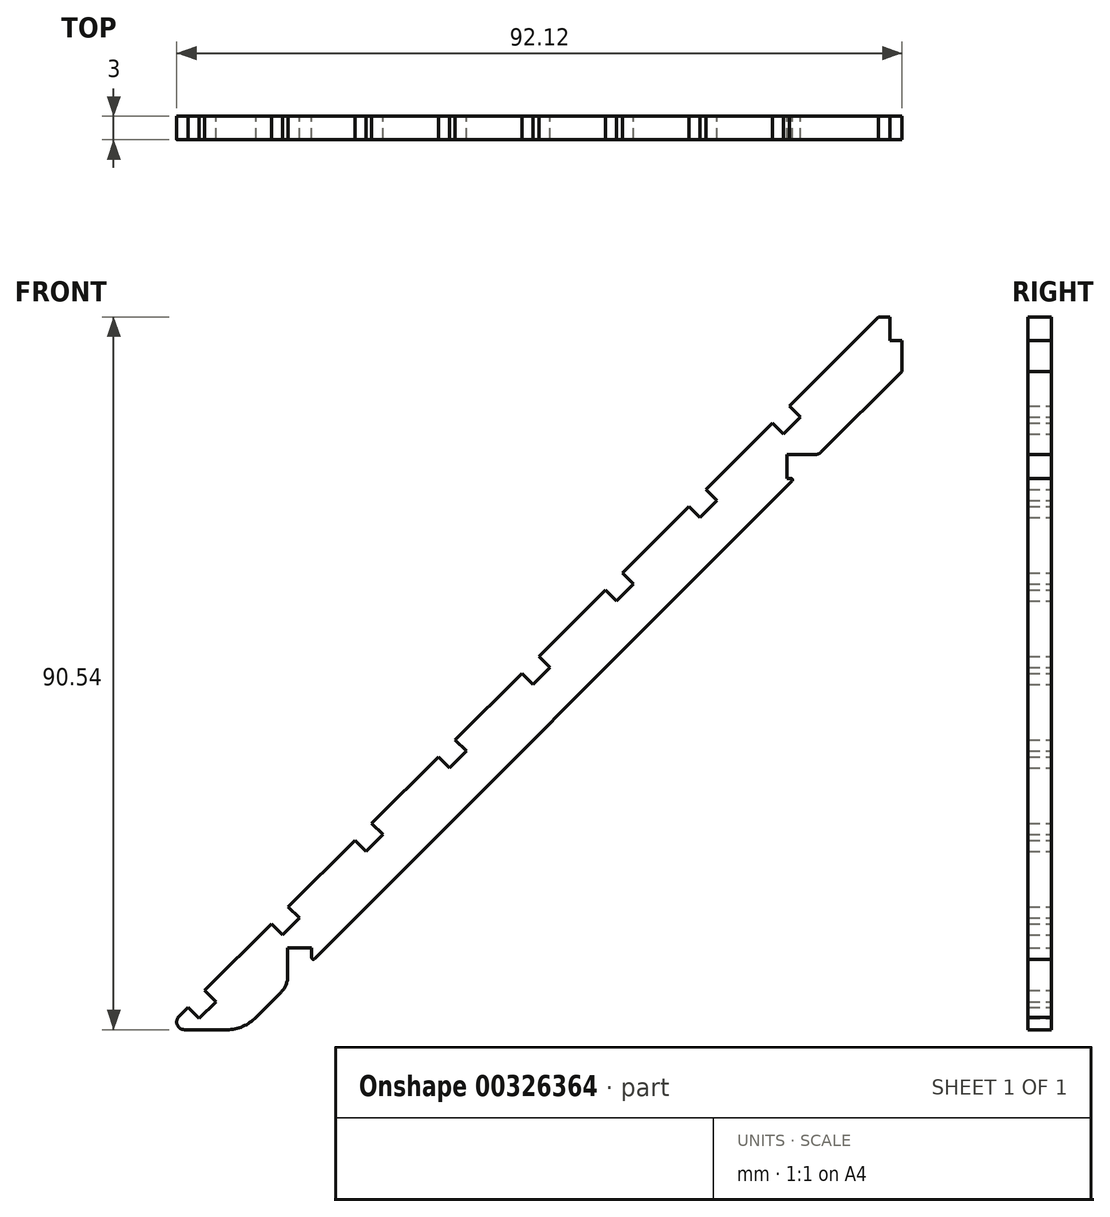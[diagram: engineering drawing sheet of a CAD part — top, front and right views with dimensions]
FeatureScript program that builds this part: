
annotation { "Feature Type Name" : "Feature", "Feature Type Description" : "" }
export const myFeature = defineFeature(function(context is Context, id is Id, definition is map)
    precondition{}
    {
        {
            var Q0;
            Q0=qCreatedBy(makeId("Front.planeOp"),FACE);
            var sketch = newSketch(context, id + "F0", { "sketchPlane" : qUnion([Q0])});
            skLineSegment(sketch, "E0", {"start": v(-77.95, 1.26) * mm, "end": v(-69.5, 9.72) * mm});
            skLineSegment(sketch, "E1", {"start": v(-80.1, -0.89) * mm, "end": v(-88.56, -9.34) * mm});
            skLineSegment(sketch, "E2", {"start": v(-85.7, -14.32) * mm, "end": v(-91.12, -14.32) * mm});
            skLineSegment(sketch, "E3", {"start": v(-90.7, -11.5) * mm, "end": v(-89.3, -12.9) * mm});
            skLineSegment(sketch, "E4", {"start": v(-89.3, -12.9) * mm, "end": v(-87.14, -10.76) * mm});
            skLineSegment(sketch, "E5", {"start": v(-78.69, -2.3) * mm, "end": v(-76.54, -0.15) * mm});
            skLineSegment(sketch, "E6", {"start": v(-80.1, -0.89) * mm, "end": v(-78.69, -2.3) * mm});
            skPoint(sketch, "E7", {"position": v(-69.5, 9.72) * mm});
            skPoint(sketch, "E8", {"position": v(-58.89, 20.33) * mm});
            skPoint(sketch, "E9", {"position": v(-48.28, 30.93) * mm});
            skPoint(sketch, "E10", {"position": v(-37.67, 41.54) * mm});
            skPoint(sketch, "E11", {"position": v(-27.07, 52.15) * mm});
            skPoint(sketch, "E12", {"position": v(-16.46, 62.75) * mm});
            skLineSegment(sketch, "E13", {"start": v(-87.14, -10.76) * mm, "end": v(-88.56, -9.34) * mm});
            skLineSegment(sketch, "E14", {"start": v(-69.5, 9.72) * mm, "end": v(-68.08, 8.3) * mm});
            skLineSegment(sketch, "E15", {"start": v(-58.89, 20.33) * mm, "end": v(-57.47, 18.91) * mm});
            skLineSegment(sketch, "E16", {"start": v(-48.28, 30.93) * mm, "end": v(-46.87, 29.52) * mm});
            skLineSegment(sketch, "E17", {"start": v(-37.67, 41.54) * mm, "end": v(-36.26, 40.12) * mm});
            skLineSegment(sketch, "E18", {"start": v(-27.07, 52.15) * mm, "end": v(-25.65, 50.73) * mm});
            skLineSegment(sketch, "E19", {"start": v(-16.46, 62.75) * mm, "end": v(-15.05, 61.34) * mm});
            skLineSegment(sketch, "E20", {"start": v(-77.95, 1.26) * mm, "end": v(-76.54, -0.15) * mm});
            skLineSegment(sketch, "E21", {"start": v(-67.34, 11.87) * mm, "end": v(-65.93, 10.45) * mm});
            skLineSegment(sketch, "E22", {"start": v(-56.74, 22.48) * mm, "end": v(-55.32, 21.06) * mm});
            skLineSegment(sketch, "E23", {"start": v(-46.13, 33.08) * mm, "end": v(-44.72, 31.67) * mm});
            skLineSegment(sketch, "E24", {"start": v(-35.53, 43.69) * mm, "end": v(-34.11, 42.27) * mm});
            skLineSegment(sketch, "E25", {"start": v(-24.92, 54.3) * mm, "end": v(-23.5, 52.88) * mm});
            skLineSegment(sketch, "E26", {"start": v(-14.31, 64.9) * mm, "end": v(-12.9, 63.49) * mm});
            skLineSegment(sketch, "E27", {"start": v(-3, 76.22) * mm, "end": v(-1.52, 76.22) * mm});
            skLineSegment(sketch, "E28", {"start": v(-1.52, 73.21) * mm, "end": v(-1.52, 76.22) * mm});
            skLineSegment(sketch, "E29", {"start": v(0, 69.31) * mm, "end": v(0, 73.21) * mm});
            skLineSegment(sketch, "E30", {"start": v(-1.52, 73.21) * mm, "end": v(0, 73.21) * mm});
            skLineSegment(sketch, "E31.trimOffspring", {"start": v(-90.7, -11.5) * mm, "end": v(-91.83, -12.62) * mm});
            skLineSegment(sketch, "E32.trimOffspring", {"start": v(-68.08, 8.3) * mm, "end": v(-65.93, 10.45) * mm});
            skLineSegment(sketch, "E33.trimOffspring", {"start": v(-67.34, 11.87) * mm, "end": v(-58.89, 20.33) * mm});
            skLineSegment(sketch, "E34.trimOffspring", {"start": v(-57.47, 18.91) * mm, "end": v(-55.32, 21.06) * mm});
            skLineSegment(sketch, "E35.trimOffspring", {"start": v(-56.74, 22.48) * mm, "end": v(-48.28, 30.93) * mm});
            skLineSegment(sketch, "E36.trimOffspring", {"start": v(-46.87, 29.52) * mm, "end": v(-44.72, 31.67) * mm});
            skLineSegment(sketch, "E37.trimOffspring", {"start": v(-46.13, 33.08) * mm, "end": v(-37.67, 41.54) * mm});
            skLineSegment(sketch, "E38.trimOffspring", {"start": v(-36.26, 40.12) * mm, "end": v(-34.11, 42.27) * mm});
            skLineSegment(sketch, "E39.trimOffspring", {"start": v(-35.53, 43.69) * mm, "end": v(-27.07, 52.15) * mm});
            skLineSegment(sketch, "E40.trimOffspring", {"start": v(-25.65, 50.73) * mm, "end": v(-23.5, 52.88) * mm});
            skLineSegment(sketch, "E41.trimOffspring", {"start": v(-24.92, 54.3) * mm, "end": v(-16.46, 62.75) * mm});
            skLineSegment(sketch, "E42.trimOffspring", {"start": v(-15.05, 61.34) * mm, "end": v(-12.9, 63.49) * mm});
            skLineSegment(sketch, "E43.trimOffspring", {"start": v(-14.31, 64.9) * mm, "end": v(-3, 76.22) * mm});
            skLineSegment(sketch, "E44", {"start": v(-70.55, -1.23) * mm, "end": v(-13.95, 55.36) * mm});
            skPoint(sketch, "E45.visualSharp", {"position": v(-93.54, -14.32) * mm});
            skArc(sketch, "E45.filletArc", {"start": v(-91.83, -12.62) * mm, "mid": v(-92.05, -13.7) * mm, "end": v(-91.12, -14.32) * mm});
            skPoint(sketch, "E46.visualSharp", {"position": v(-83.45, -14.32) * mm});
            skArc(sketch, "E46.filletArc", {"start": v(-85.7, -14.32) * mm, "mid": v(-83.72, -13.91) * mm, "end": v(-82.07, -12.75) * mm});
            skPoint(sketch, "E47", {"position": v(-78, -3.95) * mm});
            skLineSegment(sketch, "E48", {"start": v(-82.07, -12.75) * mm, "end": v(-78.89, -9.57) * mm});
            skLineSegment(sketch, "E49", {"start": v(-78, -3.95) * mm, "end": v(-78, -7.45) * mm});
            skLineSegment(sketch, "E50", {"start": v(-70.55, -1.23) * mm, "end": v(-74.63, -5.31) * mm});
            skLineSegment(sketch, "E51", {"start": v(-78, -3.95) * mm, "end": v(-74.97, -3.95) * mm});
            skLineSegment(sketch, "E52", {"start": v(-74.97, -3.95) * mm, "end": v(-74.97, -5.17) * mm});
            skPoint(sketch, "E53.endSnap0", {"position": v(-76.49, -3.95) * mm});
            skPoint(sketch, "E54", {"position": v(-73.26, -3.95) * mm});
            skPoint(sketch, "E55.visualSharp", {"position": v(-78, -8.7) * mm});
            skArc(sketch, "E55.filletArc", {"start": v(-78.89, -9.57) * mm, "mid": v(-78.24, -8.6) * mm, "end": v(-78, -7.45) * mm});
            skPoint(sketch, "E56.visualSharp", {"position": v(-74.97, -5.66) * mm});
            skArc(sketch, "E56.filletArc", {"start": v(-74.97, -5.17) * mm, "mid": v(-74.85, -5.36) * mm, "end": v(-74.63, -5.31) * mm});
            skPoint(sketch, "E57", {"position": v(-5.02, 64.3) * mm});
            skLineSegment(sketch, "E58.trimOffspring", {"start": v(-1.98, 67.33) * mm, "end": v(0, 69.31) * mm});
            skLineSegment(sketch, "E59", {"start": v(-5.36, 63.95) * mm, "end": v(-1.98, 67.33) * mm});
            skPoint(sketch, "E60", {"position": v(-14.61, 55.7) * mm});
            skPoint(sketch, "E61", {"position": v(-14.61, 58.74) * mm});
            skLineSegment(sketch, "E62", {"start": v(-14.61, 58.74) * mm, "end": v(-10.98, 58.74) * mm});
            skLineSegment(sketch, "E63", {"start": v(-14.61, 58.74) * mm, "end": v(-14.61, 55.7) * mm});
            skLineSegment(sketch, "E64", {"start": v(-14.61, 55.7) * mm, "end": v(-14.1, 55.7) * mm});
            skLineSegment(sketch, "E65.trimOffspring", {"start": v(-10.28, 59.04) * mm, "end": v(-5.36, 63.95) * mm});
            skPoint(sketch, "E66.visualSharp", {"position": v(-13.61, 55.7) * mm});
            skArc(sketch, "E66.filletArc", {"start": v(-13.95, 55.36) * mm, "mid": v(-13.9, 55.58) * mm, "end": v(-14.1, 55.7) * mm});
            skPoint(sketch, "E67.visualSharp", {"position": v(-10.57, 58.74) * mm});
            skArc(sketch, "E67.filletArc", {"start": v(-10.98, 58.74) * mm, "mid": v(-10.6, 58.82) * mm, "end": v(-10.28, 59.04) * mm});
            skSolve(sketch);
        }
        {
            var Q0;
            Q0=makeQuery(id+"F0.imprint","IMPRINT",FACE,{"disambiguationData":[TD([[makeQuery(id+"F0.imprint","IMPRINT",EDGE,{"derivedFrom":sQuery(id+"F0.wireOp",EDGE,"E0")}),-1.0]])]});
            extrude(context, id + "F1", {"entities" : qUnion([Q0]), "depth" : 3 * mm});
        }
    });
